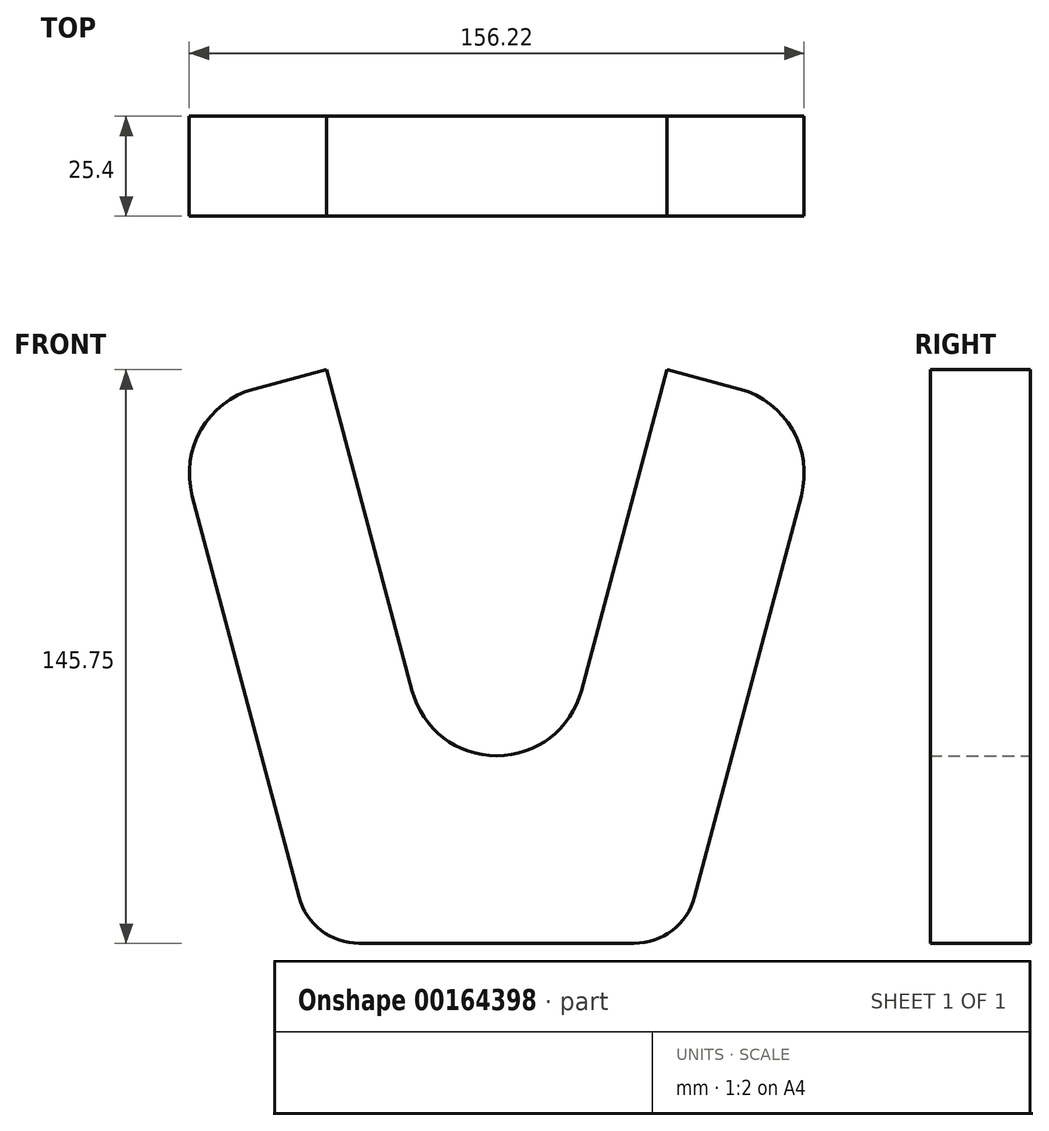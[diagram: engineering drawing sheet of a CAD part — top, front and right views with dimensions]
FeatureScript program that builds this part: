
annotation { "Feature Type Name" : "Feature", "Feature Type Description" : "" }
export const myFeature = defineFeature(function(context is Context, id is Id, definition is map)
    precondition{}
    {
        {
            var Q0;
            Q0=qCreatedBy(makeId("Front.planeOp"),FACE);
            var sketch = newSketch(context, id + "F0", { "sketchPlane" : qUnion([Q0])});
            skPoint(sketch, "E0", {"position": v(-34.93, -53.98) * mm});
            skPoint(sketch, "E1", {"position": v(0, 0) * mm});
            skPoint(sketch, "E2", {"position": v(34.93, -69.85) * mm});
            skPoint(sketch, "E3", {"position": v(55.88, 49.53) * mm});
            skPoint(sketch, "E4", {"position": v(-55.88, 49.53) * mm});
            skLineSegment(sketch, "E5", {"start": v(-34.93, -69.85) * mm, "end": v(34.93, -69.85) * mm});
            skLineSegment(sketch, "E6", {"start": v(-50.27, -58.05) * mm, "end": v(-77.36, 43.82) * mm});
            skArc(sketch, "E7", {"start": v(-34.93, -69.85) * mm, "mid": v(-44.6, -66.56) * mm, "end": v(-50.27, -58.05) * mm});
            skArc(sketch, "E8", {"start": v(34.93, -69.85) * mm, "mid": v(44.6, -66.56) * mm, "end": v(50.27, -58.05) * mm});
            skLineSegment(sketch, "E9", {"start": v(50.27, -58.05) * mm, "end": v(77.36, 43.82) * mm});
            skArc(sketch, "E10", {"start": v(77.36, 43.82) * mm, "mid": v(75.1, 60.68) * mm, "end": v(61.6, 71) * mm});
            skArc(sketch, "E11", {"start": v(-61.6, 71) * mm, "mid": v(-75.1, 60.68) * mm, "end": v(-77.36, 43.82) * mm});
            skLineSegment(sketch, "E12", {"start": v(21.48, -5.71) * mm, "end": v(43.18, 75.9) * mm});
            skLineSegment(sketch, "E13", {"start": v(43.18, 75.9) * mm, "end": v(61.6, 71) * mm});
            skLineSegment(sketch, "E14", {"start": v(-61.6, 71) * mm, "end": v(-43.18, 75.9) * mm});
            skLineSegment(sketch, "E15", {"start": v(-43.18, 75.9) * mm, "end": v(-21.48, -5.71) * mm});
            skArc(sketch, "E16", {"start": v(-21.48, -5.71) * mm, "mid": v(0, -22.23) * mm, "end": v(21.48, -5.71) * mm});
            skSolve(sketch);
        }
        {
            var Q0;
            Q0=makeQuery(id+"F0.imprint","IMPRINT",FACE,{"disambiguationData":[TD([[makeQuery(id+"F0.imprint","IMPRINT",EDGE,{"derivedFrom":sQuery(id+"F0.wireOp",EDGE,"E5")}),1.0]])]});
            extrude(context, id + "F1", {"entities" : qUnion([Q0]), "depth" : 25.4 * mm});
        }
    });
